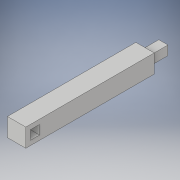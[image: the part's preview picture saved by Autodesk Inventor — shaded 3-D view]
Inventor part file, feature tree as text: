
AUTODESK INVENTOR PART (.ipt)
format: ipt  version: 2017 (Build 210142000, 142)  size: 114,688 bytes
history: native  units: in
note: dims shown in document units (in); Inventor stores cm internally (conversion verified against a paired STEP export)
features: sketch x3, extrude x2, projected_geometry x1
ambient origin geometry x8: Origin, YZ Plane, XZ Plane, XY Plane, X Axis, Y Axis, Z Axis, Center Point
bodies: Solid1 (feature_tree)
feature tree (6):
  extrude  "Extrusion1"  Depth=8.0in
  sketch  "Sketch2"  dims[d2=0.5in d3=0.5in]
  extrude  "Extrusion2"  Depth=0.5in
  sketch  "Sketch1"  dims[d0=1.0in d1=8.0in]
  sketch  "Sketch3"  dims[d4=0.25in d5=0.25in d6=1.0in d7=0.0in d8=0.5in d9=0.5in d10=0.25in d11=0.25in d12=1.0in d13=0.0in]
  projected_geometry  "Projected Loop1"
